# Revit family: Faucet-Bath_Filler-KOHLER-PURIST-K-10129T_1
name_source: partatom
category: Plumbing Fixtures
revit_build: Autodesk Revit 2017 (Build: 20160225_1515(x64)
units: mm (PartAtom-declared; Revit-internal decimal feet)

## family parameters
Cut with Voids When Loaded = No
Host = Face
OmniClass Number = 23.31.11.00
OmniClass Title = Faucets
Part Type = Normal
Room Calculation Point = No
Round Connector Dimension = Use Diameter
Shared = No

## types (4) — shared parameters
ADA Compliant = No
Assembly Code = D2010
CW Connection = Yes
Cold Water Inlet = Cold Water Inlet
Date Modified = 02/24/2021
Default Elevation = 0"
Drain Included = No
Flow Rate = 3 GPM
HW Connection = Yes
Handle Clearance = 5 13/16"
Hot Water Inlet = Hot Water Inlet
Length = 12 1/16"
Manufacturer = KOHLER Co.
Master Format 2014 = 22 41 39
Master Format 2014 Name = Residential Faucets, Supplies, and Trim
Material = Premium Metal Construction
Pressure = 80.00 psi
Product Name = Purist
Spout Reach = 12 1/16"
URL = http://www.kohler.com.cn
Vent Connection = No
Waste Connection = No
Waste Water Outlet = Waste Water Outlet
WaterSense Certified = No
Width = 7 15/16"

## per-type parameters (varying)
| type | B4 | C4 | Description | Finish | Height | Model | Type |
| B4,CP-Polished Chrome | Yes | No | Purist Floor Mount Bath Filler | Kohler-Metal-CP-Polished_Chrome | 36" | K-10129T-B4-CP | 1 |
| B4,RGD-Rose Gold | Yes | No | Purist Floor Mount Bath Filler | Kohler-Metal-RGD-Rose_Gold | 36" | K-10129T-B4-RGD | 2 |
| C4,CP-Polished Chrome | No | Yes | Purist Floor Mount Bath Shower Faucet | Kohler-Metal-CP-Polished_Chrome | 37 1/16" | K-10129T-C4-CP | 3 |
| C4,RGD-Rose Gold | No | Yes | Purist Floor Mount Bath Shower Faucet | Kohler-Metal-RGD-Rose_Gold | 37 1/16" | K-10129T-C4-RGD | 4 |

## geometry (parser evidence)
native form markers: Sweep x5
no freeform markers — native parametric forms only
